# Revit family: HOB_GEN_Noosa_Standard_Instance
name_source: partatom
category: Generic Models
units: mm (PartAtom-declared; Revit-internal decimal feet)

## family parameters
Always vertical = Yes
Can host rebar = No
Cut with Voids When Loaded = No
Maintain Annotation Orientation = No
Part Type = Normal
Room Calculation Point = No
Round Connector Dimension = Use Diameter
Shared = Yes
Work Plane-Based = No

## types (5) — shared parameters
BattenSpacing = 50 mm  [stored 0.164042 ft]
Cost = 286 $
Description = The Torquay design features smaller square bamboo slats that are mounted more closely together – just 8 mm apart.
Manufacturer = HOB
MaxHeight = 1800 mm  [stored 5.90551 ft]
MaxWidth = 400 mm  [stored 1.31234 ft]
Model = Torquay
PanelCost = 300 $
Support Rail Material = HOB_Black
zero-valued in all types: Default Elevation

## per-type parameters (varying)
| type | BattenDepth | BattenWidth | Battens Material | BattensBottomOffset | BattensTopOffset | RailBottomOffset | RailTopOffset | SideOffset | URL |
| Torquay_W400xH1860 | 20 mm  [stored 0.0656168 ft] | 20 mm  [stored 0.0656168 ft] | Bamboo_horizontalGrain | 0 mm  [stored 0 ft] | 0 mm  [stored 0 ft] | 150 mm | 150 mm | 25 mm  [stored 0.082021 ft] | https://houseofbamboo.com.au |
| Torquay_W392xH2100-R | 0 mm  [stored 0 ft] | 0 mm  [stored 0 ft] | HOB_Natural Oak | 30 mm  [stored 0.0984252 ft] | 29 mm | 107 mm | 106 mm | 7 mm  [stored 0.0229659 ft] | https://houseofbamboo.com.au |
| Torquay_W392xH1800-R | 0 mm  [stored 0 ft] | 0 mm  [stored 0 ft] | HOB_Natural Oak | 30 mm  [stored 0.0984252 ft] | 29 mm | 107 mm | 106 mm | 7 mm  [stored 0.0229659 ft] | https://houseofbamboo.com.au |
| Torquay_W392xH2400-R | 0 mm  [stored 0 ft] | 0 mm  [stored 0 ft] | HOB_Natural Oak | 30 mm  [stored 0.0984252 ft] | 29 mm | 107 mm | 106 mm | 7 mm  [stored 0.0229659 ft] | https://houseofbamboo.com.au |
| Torquay_W392xH2500 | 0 mm  [stored 0 ft] | 0 mm  [stored 0 ft] | HOB_Natural Oak | 30 mm  [stored 0.0984252 ft] | 29 mm | 107 mm | 106 mm | 7 mm  [stored 0.0229659 ft] | "https://houseofbamboo.com.au |

note: [stored X ft] marks values corroborated as IEEE doubles in the binary element streams (Revit-internal decimal feet)

## geometry (parser evidence)
native form markers: Sweep x12
no freeform markers — native parametric forms only
